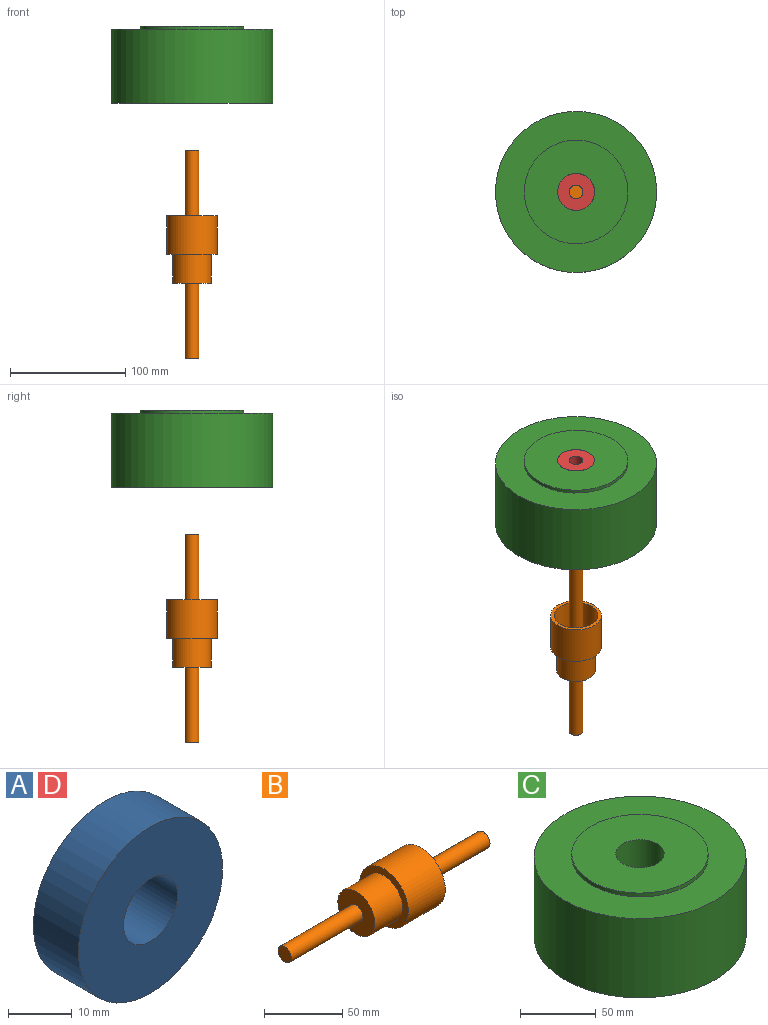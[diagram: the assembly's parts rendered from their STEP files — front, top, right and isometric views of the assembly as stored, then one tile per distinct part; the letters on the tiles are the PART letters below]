
ASSEMBLY  parts=4 mates=3
PART A: 4 faces, bbox 32x10x32 mm
  f0: cylinder r=6mm len=12mm, axis (0,1,0), area 377mm2, adj f2,f3
  f1: cylinder r=16mm len=32mm, axis (0,1,0), area 1005.3mm2, adj f2,f3
  f2: plane 32x32mm, normal (0,-1,0), area 691.2mm2, adj f0,f1
  f3: plane 32x32mm, normal (0,1,0), area 691.2mm2, adj f0,f1
PART B: 11 faces, bbox 180x44x44 mm
  f0: plane 44x44mm, normal (-1,0,0), area 639.1mm2, adj f1,f10
  f1: cylinder r=16.75mm len=33.5mm, axis (-1,0,0), area 2631.1mm2, adj f0,f2
  f2: plane 33.5x33.5mm, normal (-1,0,0), area 768.3mm2, adj f1,f3
  f3: cylinder r=6mm len=65mm, axis (-1,0,0), area 2450.4mm2, adj f2,f4
  f4: plane 12x12mm, normal (-1,0,0), area 113.1mm2, adj f3
  f5: plane 12x12mm, normal (1,0,0), area 113.1mm2, adj f6
  f6: cylinder r=6mm len=87mm, axis (-1,0,0), area 3279.8mm2, adj f5,f7
  f7: plane 38x38mm, normal (1,0,0), area 1021mm2, adj f6,f8
  f8: cylinder r=19mm len=38mm, axis (-1,0,0), area 3641.1mm2, adj f7,f9
  f9: plane 44x44mm, normal (1,0,0), area 386.4mm2, adj f8,f10
  f10: cylinder r=22mm len=44mm, axis (-1,0,0), area 4630.7mm2, adj f0,f9
PART C: 90 faces, bbox 140x140x67 mm
  f0: cylinder r=68mm len=136mm, axis (0,0,-1), area 4605.4mm2, adj f1,f2,f4,f6,f7,f8,f11,f14
  f1: plane 56x5.65mm, normal (0.97,0.24,0), area 325.8mm2, adj f0,f2,f86,f89
  f2: plane 136x135.99mm, normal (0,0,-1), area 2447.8mm2, adj f0,f1,f3,f4,f5,f6,f7,f8
  f3: plane 56x11.19mm, normal (-0.66,0.75,0), area 837.5mm2, adj f2,f82,f87,f89
  f4: plane 56x4.35mm, normal (-0.75,-0.66,0), area 325.8mm2, adj f0,f2,f88,f89
  f5: plane 56x14.52mm, normal (-0.24,0.97,0), area 837.5mm2, adj f2,f36,f87,f89
  f6: plane 56x4.79mm, normal (0.57,0.82,0), area 325.8mm2, adj f0,f2,f83,f89
  f7: plane 56x4.35mm, normal (0.75,0.66,0), area 325.8mm2, adj f0,f2,f81,f89
  f8: plane 56x4.79mm, normal (0.57,-0.82,0), area 325.8mm2, adj f0,f2,f78,f89
  f9: plane 56x13.98mm, normal (0.94,0.35,0), area 837.5mm2, adj f2,f10,f77,f89
  f10: plane 56x14.85mm, normal (0.99,0.12,0), area 837.5mm2, adj f2,f9,f12,f89
  f11: plane 56x5.77mm, normal (0.12,-0.99,0), area 325.8mm2, adj f0,f2,f74,f89
  f12: plane 56x14.85mm, normal (0.99,-0.12,0), area 837.5mm2, adj f2,f10,f13,f89
  f13: plane 56x13.98mm, normal (0.94,-0.35,0), area 837.5mm2, adj f2,f12,f15,f89
  f14: plane 56x5.44mm, normal (-0.35,-0.94,0), area 325.8mm2, adj f0,f2,f71,f89
  f15: plane 56x12.31mm, normal (0.82,-0.57,0), area 837.5mm2, adj f2,f13,f65,f89
  f16: plane 56x5.65mm, normal (-0.97,0.24,0), area 325.8mm2, adj f0,f2,f67,f89
  f17: plane 56x14.52mm, normal (0.24,0.97,0), area 837.5mm2, adj f2,f36,f69,f89
  f18: plane 56x4.79mm, normal (-0.57,-0.82,0), area 325.8mm2, adj f0,f2,f70,f89
  f19: plane 56x4.35mm, normal (-0.75,-0.66,0), area 325.8mm2, adj f0,f2,f66,f89
  f20: plane 56x13.24mm, normal (0.46,-0.89,0), area 837.5mm2, adj f2,f22,f65,f89
  f21: plane 56x5.15mm, normal (-0.89,-0.46,0), area 325.8mm2, adj f0,f2,f64,f89
  f22: plane 56x14.52mm, normal (0.24,-0.97,0), area 837.5mm2, adj f2,f20,f61,f89
  f23: plane 56x5.65mm, normal (-0.97,-0.24,0), area 325.8mm2, adj f0,f2,f63,f89
  f24: plane 56x5.82mm, normal (-1,0,0), area 325.8mm2, adj f0,f2,f62,f89
  f25: plane 56x14.52mm, normal (-0.24,-0.97,0), area 837.5mm2, adj f2,f26,f61,f89
  f26: plane 56x13.24mm, normal (-0.46,-0.89,0), area 837.5mm2, adj f2,f25,f28,f89
  f27: plane 56x5.15mm, normal (-0.89,0.46,0), area 325.8mm2, adj f0,f2,f58,f89
  f28: plane 56x11.19mm, normal (-0.66,-0.75,0), area 837.5mm2, adj f2,f26,f29,f89
  f29: plane 56x12.31mm, normal (-0.82,-0.57,0), area 837.5mm2, adj f2,f28,f31,f89
  f30: plane 56x4.79mm, normal (-0.57,0.82,0), area 325.8mm2, adj f0,f2,f55,f89
  f31: plane 56x13.98mm, normal (-0.94,-0.35,0), area 837.5mm2, adj f2,f29,f52,f89
  f32: plane 56x5.44mm, normal (-0.35,0.94,0), area 325.8mm2, adj f0,f2,f54,f89
  f33: plane 56x5.44mm, normal (0.35,-0.94,0), area 325.8mm2, adj f0,f2,f53,f89
  f34: plane 56x14.85mm, normal (-0.99,0.12,0), area 837.5mm2, adj f2,f52,f84,f89
  f35: plane 56x5.77mm, normal (0.12,0.99,0), area 325.8mm2, adj f0,f2,f51,f89
  f36: plane 56x14.96mm, normal (0,1,0), area 837.5mm2, adj f2,f5,f17,f89
  f37: plane 56x5.82mm, normal (1,0,0), area 325.8mm2, adj f0,f2,f49,f89
  f38: plane 56x5.82mm, normal (-1,0,0), area 325.8mm2, adj f0,f2,f48,f89
  f39: plane 136x136mm, normal (0,0,-1), area 13392.6mm2, adj f0,f40
  f40: cylinder r=19mm len=38mm, axis (0,0,-1), area 3521.7mm2, adj f39,f41
  f41: plane 38x38mm, normal (0,0,-1), area 329.9mm2, adj f40,f42
  f42: cylinder r=16mm len=34.5mm, axis (0,0,-1), area 3468.3mm2, adj f41,f43
  f43: plane 90x90mm, normal (0,0,1), area 5557.5mm2, adj f42,f44
  f44: cylinder r=45mm len=90mm, axis (0,0,-1), area 848.2mm2, adj f43,f45
  f45: plane 140x140mm, normal (0,0,1), area 9032.1mm2, adj f44,f46
  f46: cylinder r=70mm len=140mm, axis (0,0,-1), area 28148.7mm2, adj f45,f47
  f47: plane 140x140mm, normal (0,0,-1), area 867.1mm2, adj f0,f46
  f48: plane 56x5.65mm, normal (0.97,-0.24,0), area 325.8mm2, adj f0,f2,f38,f89
  f49: plane 56x5.65mm, normal (-0.97,-0.24,0), area 325.8mm2, adj f0,f2,f37,f89
  f50: plane 56x5.77mm, normal (-0.12,-0.99,0), area 325.8mm2, adj f0,f2,f85,f89
  f51: plane 56x5.77mm, normal (0.12,-0.99,0), area 325.8mm2, adj f0,f2,f35,f89
  f52: plane 56x14.85mm, normal (-0.99,-0.12,0), area 837.5mm2, adj f2,f31,f34,f89
  f53: plane 56x5.77mm, normal (-0.12,0.99,0), area 325.8mm2, adj f0,f2,f33,f89
  f54: plane 56x4.79mm, normal (0.57,-0.82,0), area 325.8mm2, adj f0,f2,f32,f89
  f55: plane 56x4.35mm, normal (0.75,-0.66,0), area 325.8mm2, adj f0,f2,f30,f89
  f56: plane 56x4.35mm, normal (-0.75,0.66,0), area 325.8mm2, adj f0,f2,f57,f89
  f57: plane 56x5.15mm, normal (0.89,-0.46,0), area 325.8mm2, adj f0,f2,f56,f89
  f58: plane 56x5.65mm, normal (0.97,-0.24,0), area 325.8mm2, adj f0,f2,f27,f89
  f59: plane 56x5.65mm, normal (-0.97,0.24,0), area 325.8mm2, adj f0,f2,f60,f89
  f60: plane 56x5.82mm, normal (1,0,0), area 325.8mm2, adj f0,f2,f59,f89
  f61: plane 56x14.96mm, normal (0,-1,0), area 837.5mm2, adj f2,f22,f25,f89
  f62: plane 56x5.65mm, normal (0.97,0.24,0), area 325.8mm2, adj f0,f2,f24,f89
  f63: plane 56x5.15mm, normal (0.89,0.46,0), area 325.8mm2, adj f0,f2,f23,f89
  f64: plane 56x4.35mm, normal (0.75,0.66,0), area 325.8mm2, adj f0,f2,f21,f89
  f65: plane 56x11.19mm, normal (0.66,-0.75,0), area 837.5mm2, adj f2,f15,f20,f89
  f66: plane 56x4.79mm, normal (0.57,0.82,0), area 325.8mm2, adj f0,f2,f19,f89
  f67: plane 56x5.15mm, normal (0.89,-0.46,0), area 325.8mm2, adj f0,f2,f16,f89
  f68: plane 56x5.15mm, normal (-0.89,0.46,0), area 325.8mm2, adj f0,f2,f79,f89
  f69: plane 56x13.24mm, normal (0.46,0.89,0), area 837.5mm2, adj f2,f17,f80,f89
  f70: plane 56x5.44mm, normal (0.35,0.94,0), area 325.8mm2, adj f0,f2,f18,f89
  f71: plane 56x5.77mm, normal (0.12,0.99,0), area 325.8mm2, adj f0,f2,f14,f89
  f72: plane 56x5.77mm, normal (-0.12,-0.99,0), area 325.8mm2, adj f0,f2,f73,f89
  f73: plane 56x5.77mm, normal (-0.12,0.99,0), area 325.8mm2, adj f0,f2,f72,f89
  f74: plane 56x5.44mm, normal (-0.35,0.94,0), area 325.8mm2, adj f0,f2,f11,f89
  f75: plane 56x5.44mm, normal (0.35,-0.94,0), area 325.8mm2, adj f0,f2,f76,f89
  f76: plane 56x4.79mm, normal (-0.57,0.82,0), area 325.8mm2, adj f0,f2,f75,f89
  f77: plane 56x12.31mm, normal (0.82,0.57,0), area 837.5mm2, adj f2,f9,f80,f89
  f78: plane 56x4.35mm, normal (-0.75,0.66,0), area 325.8mm2, adj f0,f2,f8,f89
  f79: plane 56x4.35mm, normal (0.75,-0.66,0), area 325.8mm2, adj f0,f2,f68,f89
  f80: plane 56x11.19mm, normal (0.66,0.75,0), area 837.5mm2, adj f2,f69,f77,f89
  f81: plane 56x4.79mm, normal (-0.57,-0.82,0), area 325.8mm2, adj f0,f2,f7,f89
  f82: plane 56x12.31mm, normal (-0.82,0.57,0), area 837.5mm2, adj f2,f3,f84,f89
  f83: plane 56x5.44mm, normal (-0.35,-0.94,0), area 325.8mm2, adj f0,f2,f6,f89
  f84: plane 56x13.98mm, normal (-0.94,0.35,0), area 837.5mm2, adj f2,f34,f82,f89
  f85: plane 56x5.44mm, normal (0.35,0.94,0), area 325.8mm2, adj f0,f2,f50,f89
  f86: plane 56x5.15mm, normal (-0.89,-0.46,0), area 325.8mm2, adj f0,f1,f2,f89
  f87: plane 56x13.24mm, normal (-0.46,0.89,0), area 837.5mm2, adj f2,f3,f5,f89
  f88: plane 56x5.15mm, normal (0.89,0.46,0), area 325.8mm2, adj f0,f2,f4,f89
  f89: plane 136x135.99mm, normal (0,0,1), area 2447.8mm2, adj f0,f1,f3,f4,f5,f6,f7,f8
PART D: same geometry as A
PLACE A rot(axis=(-1,0,0),90deg) t=(-21.39,32.61,-32.61)mm
PLACE B rot(axis=(0,-1,0),90deg) t=(-21.39,32.61,-196.49)mm
PLACE C t=(-21.39,32.61,-32.61)mm
PLACE D rot(axis=(1,0,0),90deg) t=(-21.39,32.61,1.89)mm
MATE revolute D.f1 <-> C.f0  axis (0,0,1) through (-21.39,32.61,-8.11)mm
MATE slider B.f1 <-> D.f0  axis (0,0,-1) through (-21.39,32.61,-149.99)mm
MATE revolute A.f1 <-> C.f0  axis (0,0,-1) through (-21.39,32.61,-22.61)mm
